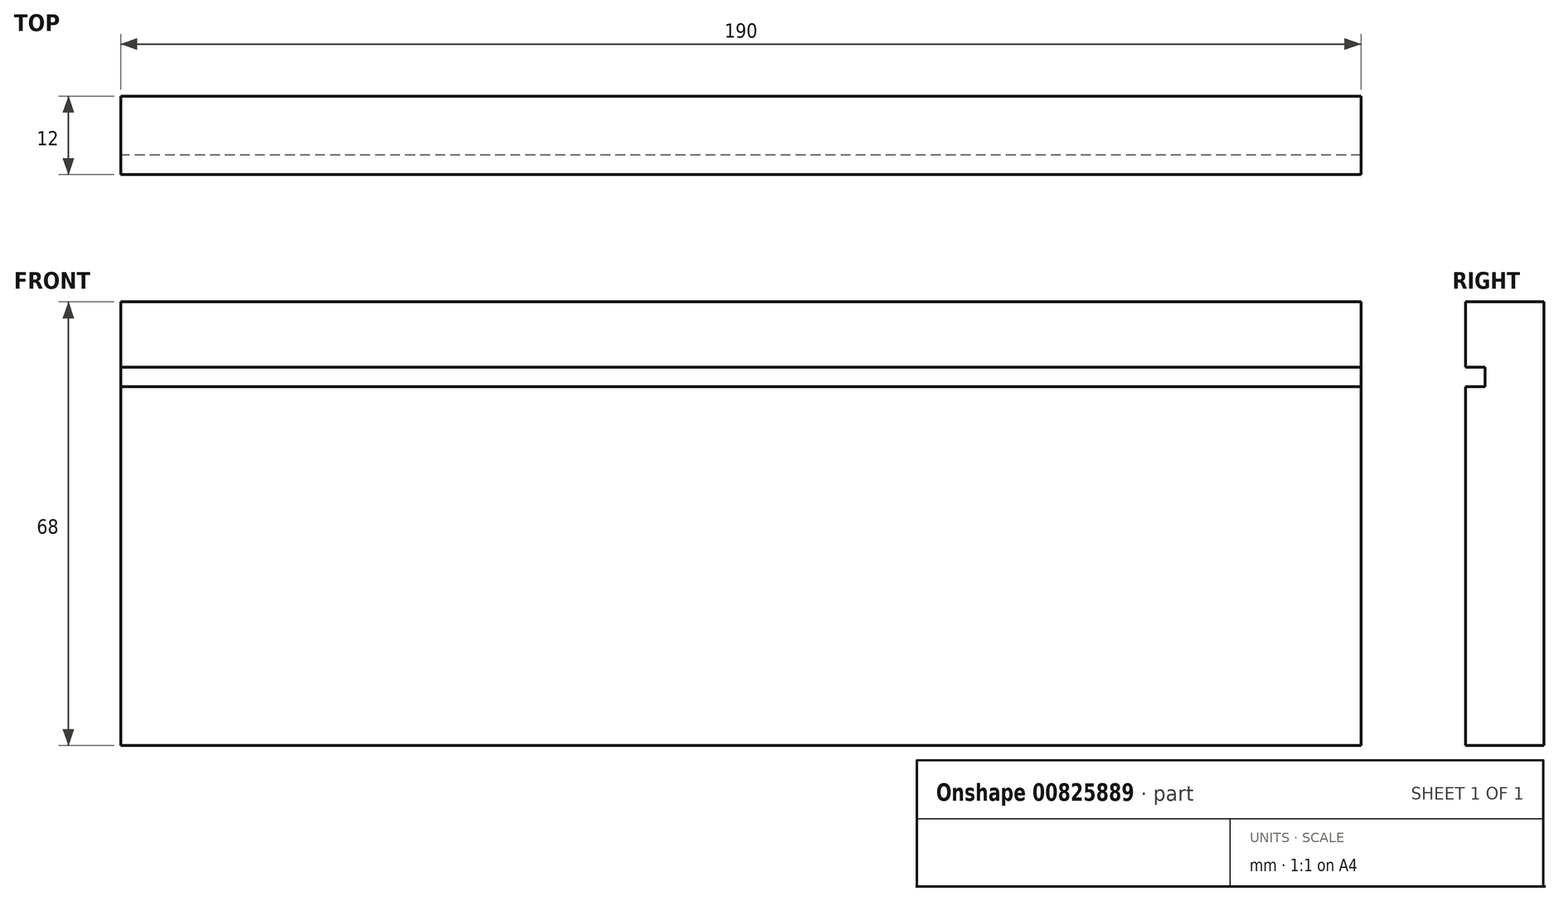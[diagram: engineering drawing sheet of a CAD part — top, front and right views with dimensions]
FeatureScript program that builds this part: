
annotation { "Feature Type Name" : "Feature", "Feature Type Description" : "" }
export const myFeature = defineFeature(function(context is Context, id is Id, definition is map)
    precondition{}
    {
        {
            var Q0;
            Q0=qCreatedBy(makeId("Right.planeOp"),FACE);
            var sketch = newSketch(context, id + "F0", { "sketchPlane" : qUnion([Q0])});
            skLineSegment(sketch, "E0.bottom", {"start": v(-54.88, -39.23) * mm, "end": v(-42.88, -39.23) * mm});
            skLineSegment(sketch, "E0.top", {"start": v(-54.88, 28.77) * mm, "end": v(-42.88, 28.77) * mm});
            skLineSegment(sketch, "E0.left", {"start": v(-54.88, -39.23) * mm, "end": v(-54.88, 15.77) * mm});
            skLineSegment(sketch, "E0.right", {"start": v(-42.88, -39.23) * mm, "end": v(-42.88, 28.77) * mm});
            skLineSegment(sketch, "E1", {"start": v(-54.88, 28.77) * mm, "end": v(-54.88, 18.77) * mm});
            skLineSegment(sketch, "E2", {"start": v(-54.88, 18.77) * mm, "end": v(-51.88, 18.77) * mm});
            skLineSegment(sketch, "E3", {"start": v(-51.88, 18.77) * mm, "end": v(-51.88, 15.77) * mm});
            skLineSegment(sketch, "E4", {"start": v(-51.88, 15.77) * mm, "end": v(-54.88, 15.77) * mm});
            skLineSegment(sketch, "E5.trimOffspring", {"start": v(-54.88, 18.77) * mm, "end": v(-54.88, 28.77) * mm});
            skSolve(sketch);
        }
        {
            var Q0;
            Q0=makeQuery(id+"F0.imprint","IMPRINT",FACE,{"disambiguationData":[TD([[makeQuery(id+"F0.imprint","IMPRINT",EDGE,{"derivedFrom":sQuery(id+"F0.wireOp",EDGE,"E0.bottom")}),1.0]])]});
            extrude(context, id + "F1", {"entities" : qUnion([Q0]), "depth" : 190 * mm, "offsetDistance" : 25.4 * mm});
        }
    });
